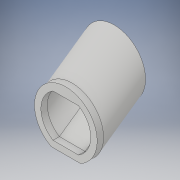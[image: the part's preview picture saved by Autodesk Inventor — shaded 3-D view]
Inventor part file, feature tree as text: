
AUTODESK INVENTOR PART (.ipt)
format: ipt  version: 2017 (Build 210142000, 142)  size: 135,168 bytes
history: native  units: in
note: dims shown in document units (in); Inventor stores cm internally (conversion verified against a paired STEP export)
features: sketch x3, plane x1, sweep x1, extrude x1
ambient origin geometry x8: Origin, YZ Plane, XZ Plane, XY Plane, X Axis, Y Axis, Z Axis, Center Point
bodies: Solid1 (feature_tree)
feature tree (6):
  sketch  "Sketch1"  dims[d0=6.6667in d1=4.0in d2=1.0in d28=8.0in]
  plane  "Work Plane2"
  sweep  "ramp"
  extrude  "connection bottom"  TaperAngle=0.0deg  [1 undecoded]
  sketch  "Sketch6"  dims[d29=0.3779in d30=0.0in d31=0.0in]
  sketch  "Sketch7"  dims[d32=1.0in d33=0.0in]
note: 1 required parameter value undecoded (feature->parameter linkage not recoverable at this tier; creation-order binding heuristic only, values carry confidence <= 0.55)
